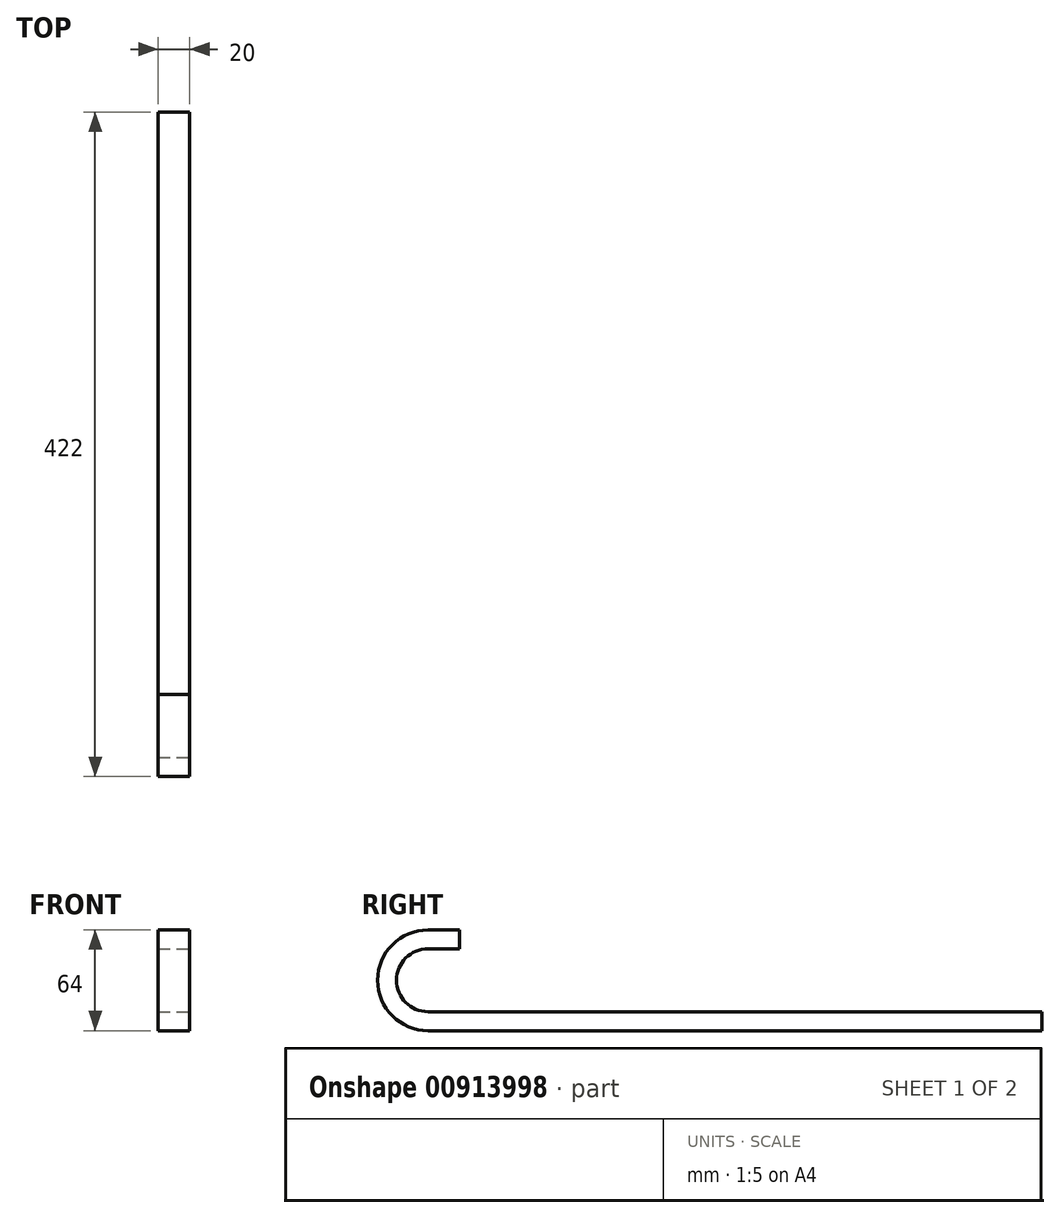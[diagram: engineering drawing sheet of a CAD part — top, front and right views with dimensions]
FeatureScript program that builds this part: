
annotation { "Feature Type Name" : "Feature", "Feature Type Description" : "" }
export const myFeature = defineFeature(function(context is Context, id is Id, definition is map)
    precondition{}
    {
        {
            var Q0;
            Q0=qCreatedBy(makeId("Right.planeOp"),FACE);
            var sketch = newSketch(context, id + "F0", { "sketchPlane" : qUnion([Q0])});
            skLineSegment(sketch, "E0", {"start": v(0, 0) * mm, "end": v(-390, 0) * mm});
            skArc(sketch, "E1", {"start": v(-390, 0) * mm, "mid": v(-422, 32) * mm, "end": v(-390, 64) * mm});
            skLineSegment(sketch, "E2", {"start": v(-390, 64) * mm, "end": v(-370, 64) * mm});
            skLineSegment(sketch, "E3", {"start": v(-370, 64) * mm, "end": v(-370, 52) * mm});
            skLineSegment(sketch, "E4", {"start": v(-370, 52) * mm, "end": v(-390, 52) * mm});
            skArc(sketch, "E5", {"start": v(-390, 52) * mm, "mid": v(-410, 32) * mm, "end": v(-390, 12) * mm});
            skLineSegment(sketch, "E6", {"start": v(-390, 12) * mm, "end": v(0, 12) * mm});
            skLineSegment(sketch, "E7", {"start": v(0, 12) * mm, "end": v(0, 0) * mm});
            skSolve(sketch);
        }
        {
            var Q0;
            Q0=makeQuery(id+"F0.imprint","IMPRINT",FACE,{"disambiguationData":[TD([[makeQuery(id+"F0.imprint","IMPRINT",EDGE,{"derivedFrom":sQuery(id+"F0.wireOp",EDGE,"E0")}),-1.0]])]});
            extrude(context, id + "F1", {"entities" : qUnion([Q0]), "oppositeDirection" : true, "depth" : 20 * mm, "offsetDistance" : 25 * mm});
        }
    });
